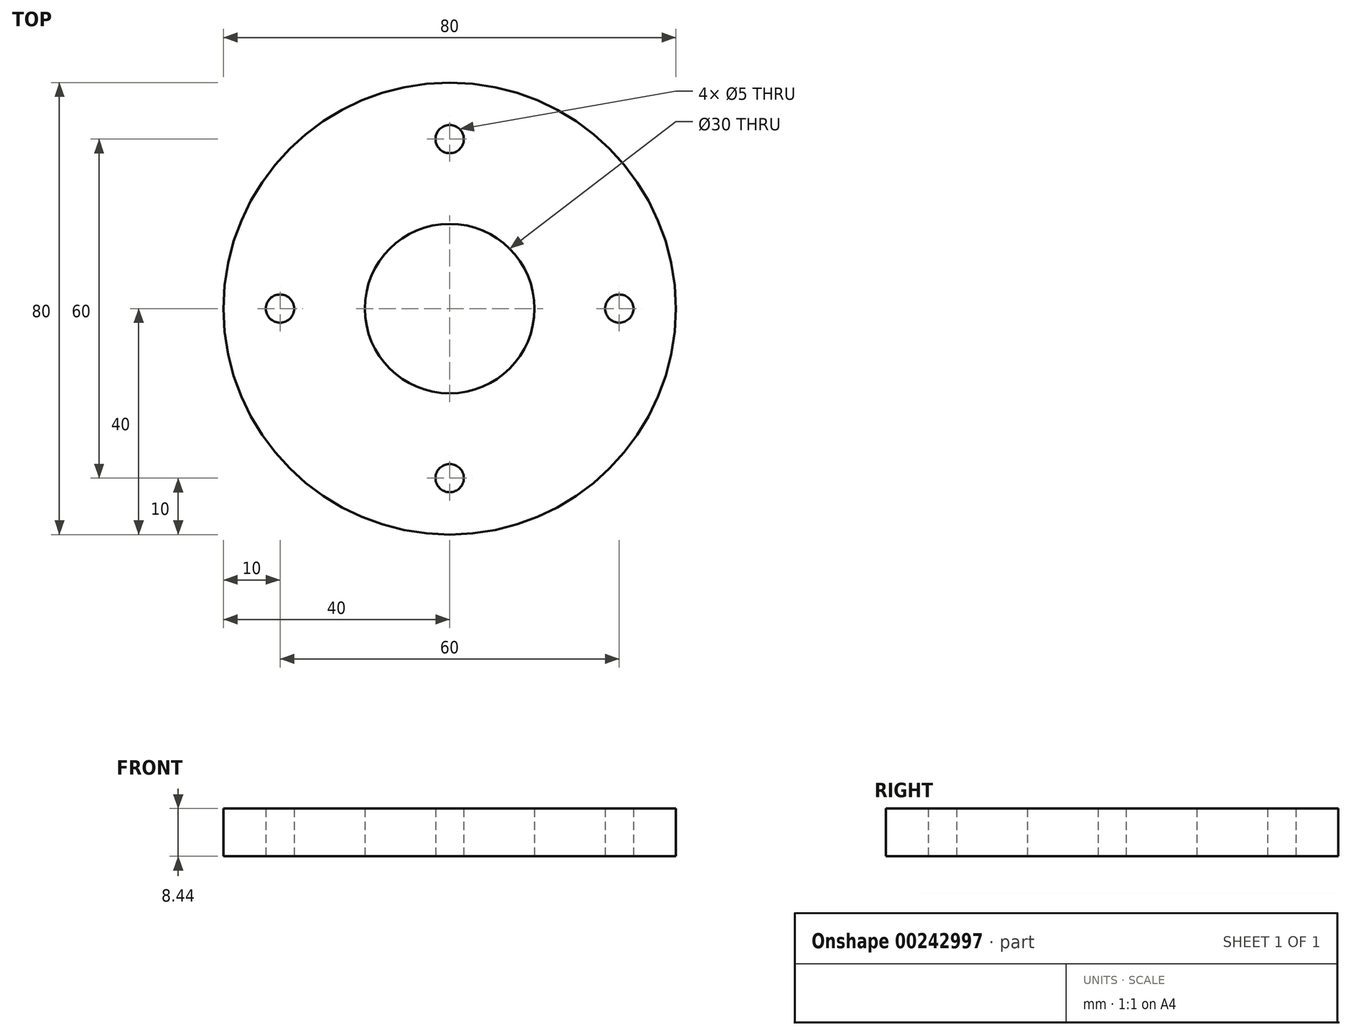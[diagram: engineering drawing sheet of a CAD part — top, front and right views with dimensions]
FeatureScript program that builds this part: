
annotation { "Feature Type Name" : "Feature", "Feature Type Description" : "" }
export const myFeature = defineFeature(function(context is Context, id is Id, definition is map)
    precondition{}
    {
        {
            var Q0;
            Q0=qCreatedBy(makeId("Top.planeOp"),FACE);
            var sketch = newSketch(context, id + "F0", { "sketchPlane" : qUnion([Q0])});
            skCircle(sketch, "E0", {"center": v(0, 0) * mm, "radius": 3.5 * mm});
            skCircle(sketch, "E1", {"center": v(0, 0) * mm, "radius": 5 * mm, "construction": true});
            skCircle(sketch, "E2", {"center": v(5, 0) * mm, "radius": 1 * mm});
            skCircle(sketch, "E3", {"center": v(0, 5) * mm, "radius": 1 * mm});
            skCircle(sketch, "E4", {"center": v(-5, 0) * mm, "radius": 1 * mm});
            skCircle(sketch, "E5", {"center": v(0, -5) * mm, "radius": 1 * mm});
            skCircle(sketch, "E6", {"center": v(0, 0) * mm, "radius": 30 * mm, "construction": true});
            skCircle(sketch, "E7", {"center": v(0, 0) * mm, "radius": 40 * mm});
            skCircle(sketch, "E8", {"center": v(30, 0) * mm, "radius": 2.5 * mm});
            skCircle(sketch, "E9", {"center": v(0, 30) * mm, "radius": 2.5 * mm});
            skCircle(sketch, "E10", {"center": v(-30, 0) * mm, "radius": 2.5 * mm});
            skCircle(sketch, "E11", {"center": v(0, -30) * mm, "radius": 2.5 * mm});
            skCircle(sketch, "E12", {"center": v(0, 0) * mm, "radius": 15 * mm});
            skSolve(sketch);
        }
        {
            var Q0;
            Q0=makeQuery(id+"F0.imprint","IMPRINT",FACE,{"disambiguationData":[TD([[makeQuery(id+"F0.imprint","IMPRINT",EDGE,{"derivedFrom":sQuery(id+"F0.wireOp",EDGE,"E7")}),1.0]])]});
            extrude(context, id + "F1", {"entities" : qUnion([Q0]), "depth" : (20 - 6 - 7 / 32 * 25.4) * mm});
        }
    });
